# Revit family: PRD_FrankeWS_StnlssStlBrckts_WallArmHolder_ZFAID700
name_source: partatom
category: Specialty Equipment
revit_build: Autodesk Revit 2018 (Build: 20190510_1515(x64)
units: mm (PartAtom-declared; Revit-internal decimal feet)

## family parameters
Always vertical = Yes
Cut with Voids When Loaded = No
OmniClass Number = 23.45.05.14.99
OmniClass Title = Other Sanitary Washing Plumbing Fixtures
Part Type = Normal
Room Calculation Point = No
Round Connector Dimension = Use Diameter
Shared = No
Work Plane-Based = Yes

## types (1)
- ZFAID700
    AssetType = Fixed
    BIMObjectName = PRD_AR_StainlessSteelBrackets_WallArmHolder_ZFAID700
    BodyMaterial = PRD_AR_Steel_PowderCoated_Green
    Category = Pr_20_85_09_81, Stainless steel brackets
    Color = green
    Default Elevation = 1219 mm
    Description = Wall arm holder for DN 20 emergency shower wall arm for installation in lightweight walls or as protection from vandals, powder-coated steel sheet, green (RAL 6032).
    DurationUnit = year
    Features = powder-coated steel sheet, green (RAL 6032)
    Finish = Powder-coated
    GrossWeight = 0.52 kg
    IfcExportAs = IfcSanitaryTerminalType
    IfcExportType = USERDEFINED
    Manufacturer = KWC Group AG
    ManufacturerName = KWC Group AG
    ManufacturerURL = www.kwc.com
    Material = Steel
    Model = ZFAID700
    ModelNumber = 2030060157
    ModelReference = ZFAID700
    NBSDescription = Stainless steel brackets
    NBSReference = 45-70-05/405
    Name = Wall arm holder ZFAID700
    NetWeight = 0.00 kg
    NominalDepth = 240 mm  [stored 0.787402 ft]
    NominalHeight = 170 mm  [stored 0.557743 ft]
    NominalLength = 0 mm  [stored 0 ft]
    NominalWidth = 270 mm  [stored 0.885827 ft]
    ProductCode = 216.0630.340
    ProductInformation = https://pim.kwc.com
    Size = 270 x 170 x 240 mm (W x H x D)
    Status = New
    TailorMade = No
    URL = www.kwc.com
    Uniclass2015Code = Pr_20_85_09_81
    Uniclass2015Title = Stainless steel brackets
    Uniclass2015Version = Products v1.17
    Version = 1
    WarrantyDurationUnit = year

note: [stored X ft] marks values corroborated as IEEE doubles in the binary element streams (Revit-internal decimal feet)

## geometry (parser evidence)
native form markers: Sweep x3
no freeform markers — native parametric forms only
